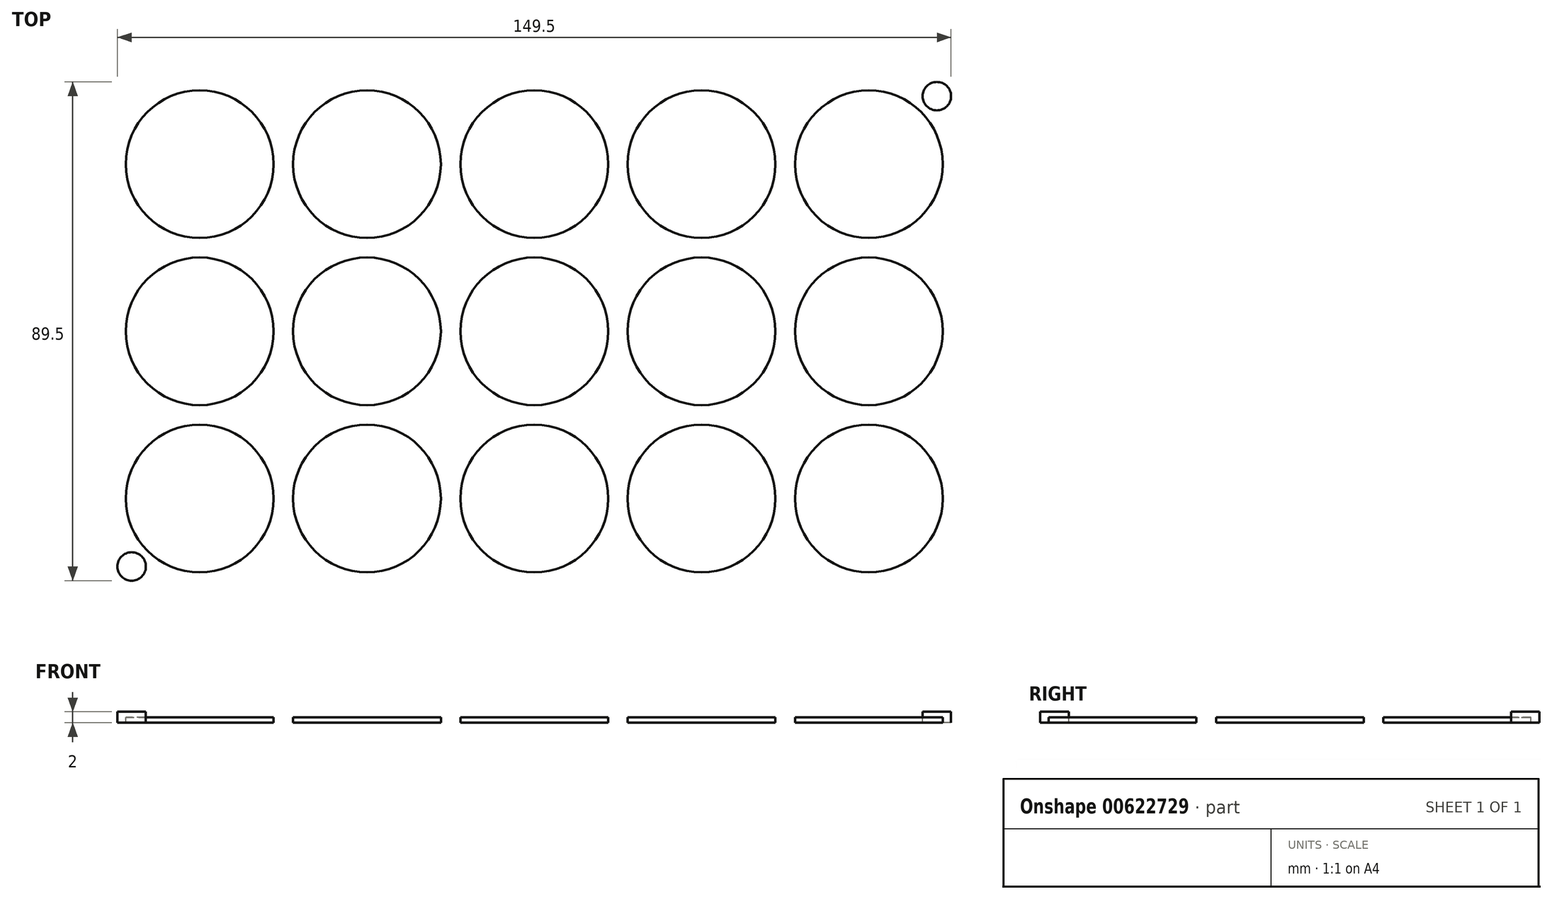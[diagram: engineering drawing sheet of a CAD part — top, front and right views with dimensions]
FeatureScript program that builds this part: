
annotation { "Feature Type Name" : "Feature", "Feature Type Description" : "" }
export const myFeature = defineFeature(function(context is Context, id is Id, definition is map)
    precondition{}
    {
        {
            var Q0;
            Q0=qCreatedBy(makeId("Top.planeOp"),FACE);
            var sketch = newSketch(context, id + "F0", { "sketchPlane" : qUnion([Q0])});
            skLineSegment(sketch, "E0.bottom", {"start": v(-76.25, 46.25) * mm, "end": v(76.25, 46.25) * mm});
            skLineSegment(sketch, "E0.top", {"start": v(-76.25, -46.25) * mm, "end": v(76.25, -46.25) * mm});
            skLineSegment(sketch, "E0.left", {"start": v(-76.25, 46.25) * mm, "end": v(-76.25, -46.25) * mm});
            skLineSegment(sketch, "E0.right", {"start": v(76.25, 46.25) * mm, "end": v(76.25, -46.25) * mm});
            skPoint(sketch, "E0.middle", {"position": v(0, 0) * mm});
            skCircle(sketch, "E1", {"center": v(-60, 30) * mm, "radius": 13.25 * mm});
            skCircle(sketch, "E2.0.1.0", {"center": v(-60, 0) * mm, "radius": 13.25 * mm});
            skCircle(sketch, "E2.0.2.0", {"center": v(-60, -30) * mm, "radius": 13.25 * mm});
            skCircle(sketch, "E2.1.0.0", {"center": v(-30, 30) * mm, "radius": 13.25 * mm});
            skCircle(sketch, "E2.1.1.0", {"center": v(-30, 0) * mm, "radius": 13.25 * mm});
            skCircle(sketch, "E2.1.2.0", {"center": v(-30, -30) * mm, "radius": 13.25 * mm});
            skCircle(sketch, "E2.2.0.0", {"center": v(0, 30) * mm, "radius": 13.25 * mm});
            skCircle(sketch, "E2.2.1.0", {"center": v(0, 0) * mm, "radius": 13.25 * mm});
            skCircle(sketch, "E2.2.2.0", {"center": v(0, -30) * mm, "radius": 13.25 * mm});
            skCircle(sketch, "E2.3.0.0", {"center": v(30, 30) * mm, "radius": 13.25 * mm});
            skCircle(sketch, "E2.3.1.0", {"center": v(30, 0) * mm, "radius": 13.25 * mm});
            skCircle(sketch, "E2.3.2.0", {"center": v(30, -30) * mm, "radius": 13.25 * mm});
            skCircle(sketch, "E2.4.0.0", {"center": v(60, 30) * mm, "radius": 13.25 * mm});
            skCircle(sketch, "E2.4.1.0", {"center": v(60, 0) * mm, "radius": 13.25 * mm});
            skCircle(sketch, "E2.4.2.0", {"center": v(60, -30) * mm, "radius": 13.25 * mm});
            skLineSegment(sketch, "E2.direction1", {"start": v(-60, 30) * mm, "end": v(-30, 30) * mm, "construction": true});
            skLineSegment(sketch, "E2.direction2", {"start": v(-60, 30) * mm, "end": v(-60, 0) * mm, "construction": true});
            skSolve(sketch);
        }
        {
            var Q0;
            Q0=makeQuery(id+"F0.imprint","IMPRINT",FACE,{"disambiguationData":[TD([[makeQuery(id+"F0.imprint","IMPRINT",EDGE,{"derivedFrom":sQuery(id+"F0.wireOp",EDGE,"E1")}),1.0]])]});
            var Q1;
            Q1=makeQuery(id+"F0.imprint","IMPRINT",FACE,{"disambiguationData":[TD([[makeQuery(id+"F0.imprint","IMPRINT",EDGE,{"derivedFrom":sQuery(id+"F0.wireOp",EDGE,"E2.1.0.0")}),1.0]])]});
            var Q2;
            Q2=makeQuery(id+"F0.imprint","IMPRINT",FACE,{"disambiguationData":[TD([[makeQuery(id+"F0.imprint","IMPRINT",EDGE,{"derivedFrom":sQuery(id+"F0.wireOp",EDGE,"E2.2.0.0")}),1.0]])]});
            var Q3;
            Q3=makeQuery(id+"F0.imprint","IMPRINT",FACE,{"disambiguationData":[TD([[makeQuery(id+"F0.imprint","IMPRINT",EDGE,{"derivedFrom":sQuery(id+"F0.wireOp",EDGE,"E2.3.0.0")}),1.0]])]});
            var Q4;
            Q4=makeQuery(id+"F0.imprint","IMPRINT",FACE,{"disambiguationData":[TD([[makeQuery(id+"F0.imprint","IMPRINT",EDGE,{"derivedFrom":sQuery(id+"F0.wireOp",EDGE,"E2.4.0.0")}),1.0]])]});
            var Q5;
            Q5=makeQuery(id+"F0.imprint","IMPRINT",FACE,{"disambiguationData":[TD([[makeQuery(id+"F0.imprint","IMPRINT",EDGE,{"derivedFrom":sQuery(id+"F0.wireOp",EDGE,"E2.4.1.0")}),1.0]])]});
            var Q6;
            Q6=makeQuery(id+"F0.imprint","IMPRINT",FACE,{"disambiguationData":[TD([[makeQuery(id+"F0.imprint","IMPRINT",EDGE,{"derivedFrom":sQuery(id+"F0.wireOp",EDGE,"E2.3.1.0")}),1.0]])]});
            var Q7;
            Q7=makeQuery(id+"F0.imprint","IMPRINT",FACE,{"disambiguationData":[TD([[makeQuery(id+"F0.imprint","IMPRINT",EDGE,{"derivedFrom":sQuery(id+"F0.wireOp",EDGE,"E0.bottom")}),-1.0]])]});
            var Q8;
            Q8=makeQuery(id+"F0.imprint","IMPRINT",FACE,{"disambiguationData":[TD([[makeQuery(id+"F0.imprint","IMPRINT",EDGE,{"derivedFrom":sQuery(id+"F0.wireOp",EDGE,"E2.1.1.0")}),1.0]])]});
            var Q9;
            Q9=makeQuery(id+"F0.imprint","IMPRINT",FACE,{"disambiguationData":[TD([[makeQuery(id+"F0.imprint","IMPRINT",EDGE,{"derivedFrom":sQuery(id+"F0.wireOp",EDGE,"E2.0.1.0")}),1.0]])]});
            var Q10;
            Q10=makeQuery(id+"F0.imprint","IMPRINT",FACE,{"disambiguationData":[TD([[makeQuery(id+"F0.imprint","IMPRINT",EDGE,{"derivedFrom":sQuery(id+"F0.wireOp",EDGE,"E2.2.1.0")}),1.0]])]});
            var Q11;
            Q11=makeQuery(id+"F0.imprint","IMPRINT",FACE,{"disambiguationData":[TD([[makeQuery(id+"F0.imprint","IMPRINT",EDGE,{"derivedFrom":sQuery(id+"F0.wireOp",EDGE,"E2.2.2.0")}),1.0]])]});
            var Q12;
            Q12=makeQuery(id+"F0.imprint","IMPRINT",FACE,{"disambiguationData":[TD([[makeQuery(id+"F0.imprint","IMPRINT",EDGE,{"derivedFrom":sQuery(id+"F0.wireOp",EDGE,"E2.1.2.0")}),1.0]])]});
            var Q13;
            Q13=makeQuery(id+"F0.imprint","IMPRINT",FACE,{"disambiguationData":[TD([[makeQuery(id+"F0.imprint","IMPRINT",EDGE,{"derivedFrom":sQuery(id+"F0.wireOp",EDGE,"E2.0.2.0")}),1.0]])]});
            var Q14;
            Q14=makeQuery(id+"F0.imprint","IMPRINT",FACE,{"disambiguationData":[TD([[makeQuery(id+"F0.imprint","IMPRINT",EDGE,{"derivedFrom":sQuery(id+"F0.wireOp",EDGE,"E2.3.2.0")}),1.0]])]});
            var Q15;
            Q15=makeQuery(id+"F0.imprint","IMPRINT",FACE,{"disambiguationData":[TD([[makeQuery(id+"F0.imprint","IMPRINT",EDGE,{"derivedFrom":sQuery(id+"F0.wireOp",EDGE,"E2.4.2.0")}),1.0]])]});
            var Q16;
            Q16=makeQuery(id+"F0.imprint","IMPRINT",FACE,{"disambiguationData":[TD([[makeQuery(id+"F0.imprint","IMPRINT",EDGE,{"derivedFrom":sQuery(id+"F0.wireOp",EDGE,"E2.3.3.0")}),1.0]])]});
            var Q17;
            Q17=makeQuery(id+"F0.imprint","IMPRINT",FACE,{"disambiguationData":[TD([[makeQuery(id+"F0.imprint","IMPRINT",EDGE,{"derivedFrom":sQuery(id+"F0.wireOp",EDGE,"E2.4.3.0")}),1.0]])]});
            var Q18;
            Q18=makeQuery(id+"F0.imprint","IMPRINT",FACE,{"disambiguationData":[TD([[makeQuery(id+"F0.imprint","IMPRINT",EDGE,{"derivedFrom":sQuery(id+"F0.wireOp",EDGE,"E2.4.4.0")}),1.0]])]});
            var Q19;
            Q19=makeQuery(id+"F0.imprint","IMPRINT",FACE,{"disambiguationData":[TD([[makeQuery(id+"F0.imprint","IMPRINT",EDGE,{"derivedFrom":sQuery(id+"F0.wireOp",EDGE,"E2.3.4.0")}),1.0]])]});
            var Q20;
            Q20=makeQuery(id+"F0.imprint","IMPRINT",FACE,{"disambiguationData":[TD([[makeQuery(id+"F0.imprint","IMPRINT",EDGE,{"derivedFrom":sQuery(id+"F0.wireOp",EDGE,"E2.2.4.0")}),1.0]])]});
            var Q21;
            Q21=makeQuery(id+"F0.imprint","IMPRINT",FACE,{"disambiguationData":[TD([[makeQuery(id+"F0.imprint","IMPRINT",EDGE,{"derivedFrom":sQuery(id+"F0.wireOp",EDGE,"E2.2.3.0")}),1.0]])]});
            var Q22;
            Q22=makeQuery(id+"F0.imprint","IMPRINT",FACE,{"disambiguationData":[TD([[makeQuery(id+"F0.imprint","IMPRINT",EDGE,{"derivedFrom":sQuery(id+"F0.wireOp",EDGE,"E2.1.4.0")}),1.0]])]});
            var Q23;
            Q23=makeQuery(id+"F0.imprint","IMPRINT",FACE,{"disambiguationData":[TD([[makeQuery(id+"F0.imprint","IMPRINT",EDGE,{"derivedFrom":sQuery(id+"F0.wireOp",EDGE,"E2.1.3.0")}),1.0]])]});
            var Q24;
            Q24=makeQuery(id+"F0.imprint","IMPRINT",FACE,{"disambiguationData":[TD([[makeQuery(id+"F0.imprint","IMPRINT",EDGE,{"derivedFrom":sQuery(id+"F0.wireOp",EDGE,"E2.0.3.0")}),1.0]])]});
            var Q25;
            Q25=makeQuery(id+"F0.imprint","IMPRINT",FACE,{"disambiguationData":[TD([[makeQuery(id+"F0.imprint","IMPRINT",EDGE,{"derivedFrom":sQuery(id+"F0.wireOp",EDGE,"E2.0.4.0")}),1.0]])]});
            extrude(context, id + "F1", {"entities" : qUnion([Q0, Q1, Q2, Q3, Q4, Q5, Q6, Q7, Q8, Q9, Q10, Q11, Q12, Q13, Q14, Q15, Q16, Q17, Q18, Q19, Q20, Q21, Q22, Q23, Q24, Q25]), "depth" : 1 * mm, "offsetDistance" : 25 * mm});
        }
        {
            var Q0;
            Q0=qSketchRegion(id+"F0",true);
            extrude(context, id + "F2", {"entities" : qUnion([Q0]), "operationType" : NewBodyOperationType.ADD, "depth" : 2 * mm, "offsetDistance" : 25 * mm});
        }
        {
            var Q0;
            Q0=makeQuery(id+"F2.opExtrude","CAP_FACE",FACE,{"disambiguationData":[OSD([sQuery(id+"F0.wireOp",EDGE,"E0.bottom"),sQuery(id+"F0.wireOp",EDGE,"E0.top"),sQuery(id+"F0.wireOp",EDGE,"E0.left"),sQuery(id+"F0.wireOp",EDGE,"E0.right"),sQuery(id+"F0.wireOp",EDGE,"E1"),sQuery(id+"F0.wireOp",EDGE,"E2.0.1.0"),sQuery(id+"F0.wireOp",EDGE,"E2.0.2.0"),sQuery(id+"F0.wireOp",EDGE,"E2.0.3.0"),sQuery(id+"F0.wireOp",EDGE,"E2.0.4.0"),sQuery(id+"F0.wireOp",EDGE,"E2.1.0.0"),sQuery(id+"F0.wireOp",EDGE,"E2.1.1.0"),sQuery(id+"F0.wireOp",EDGE,"E2.1.2.0"),sQuery(id+"F0.wireOp",EDGE,"E2.1.3.0"),sQuery(id+"F0.wireOp",EDGE,"E2.1.4.0"),sQuery(id+"F0.wireOp",EDGE,"E2.2.0.0"),sQuery(id+"F0.wireOp",EDGE,"E2.2.1.0"),sQuery(id+"F0.wireOp",EDGE,"E2.2.2.0"),sQuery(id+"F0.wireOp",EDGE,"E2.2.3.0"),sQuery(id+"F0.wireOp",EDGE,"E2.2.4.0"),sQuery(id+"F0.wireOp",EDGE,"E2.3.0.0"),sQuery(id+"F0.wireOp",EDGE,"E2.3.1.0"),sQuery(id+"F0.wireOp",EDGE,"E2.3.2.0"),sQuery(id+"F0.wireOp",EDGE,"E2.3.3.0"),sQuery(id+"F0.wireOp",EDGE,"E2.3.4.0"),sQuery(id+"F0.wireOp",EDGE,"E2.4.0.0"),sQuery(id+"F0.wireOp",EDGE,"E2.4.1.0"),sQuery(id+"F0.wireOp",EDGE,"E2.4.2.0"),sQuery(id+"F0.wireOp",EDGE,"E2.4.3.0"),sQuery(id+"F0.wireOp",EDGE,"E2.4.4.0")])],"isStart":false});
            var sketch = newSketch(context, id + "F3", { "sketchPlane" : qUnion([Q0])});
            skLineSegment(sketch, "E3", {"start": v(0, 74.2) * mm, "end": v(0, -73.43) * mm, "construction": true});
            skLineSegment(sketch, "E4", {"start": v(-81.9, 0) * mm, "end": v(78.5, 0) * mm, "construction": true});
            skCircle(sketch, "E5", {"center": v(-72.2, 42.2) * mm, "radius": 2.55 * mm});
            skCircle(sketch, "E6.MirrorC", {"center": v(72.2, 42.2) * mm, "radius": 2.55 * mm});
            skCircle(sketch, "E7.MirrorC", {"center": v(72.2, -42.2) * mm, "radius": 2.55 * mm});
            skCircle(sketch, "E8.MirrorC", {"center": v(-72.2, -42.2) * mm, "radius": 2.55 * mm});
            skCircle(sketch, "E9", {"center": v(-15, 15) * mm, "radius": 2.55 * mm});
            skCircle(sketch, "E10", {"center": v(15, -15) * mm, "radius": 2.55 * mm});
            skSolve(sketch);
        }
        {
            var Q0;
            Q0=makeQuery(id+"F3.imprint","IMPRINT",FACE,{"disambiguationData":[TD([[makeQuery(id+"F3.imprint","IMPRINT",EDGE,{"derivedFrom":sQuery(id+"F3.wireOp",EDGE,"E5")}),1.0]])]});
            var Q1;
            Q1=makeQuery(id+"F3.imprint","IMPRINT",FACE,{"disambiguationData":[TD([[makeQuery(id+"F3.imprint","IMPRINT",EDGE,{"derivedFrom":sQuery(id+"F3.wireOp",EDGE,"E6.MirrorC")}),-1.0]])]});
            var Q2;
            Q2=makeQuery(id+"F3.imprint","IMPRINT",FACE,{"disambiguationData":[TD([[makeQuery(id+"F3.imprint","IMPRINT",EDGE,{"derivedFrom":sQuery(id+"F3.wireOp",EDGE,"2e68c3d5-25cd-40bd-9945-6fc11be80f0a0.MirrorC")}),-1.0]])]});
            var Q3;
            Q3=makeQuery(id+"F3.imprint","IMPRINT",FACE,{"disambiguationData":[TD([[makeQuery(id+"F3.imprint","IMPRINT",EDGE,{"derivedFrom":sQuery(id+"F3.wireOp",EDGE,"QxaMrl3A-AtRa-trL4-GzdF-NhNgddZBNQFQ")}),1.0]])]});
            var Q4;
            Q4=makeQuery(id+"F3.imprint","IMPRINT",FACE,{"disambiguationData":[TD([[makeQuery(id+"F3.imprint","IMPRINT",EDGE,{"derivedFrom":sQuery(id+"F3.wireOp",EDGE,"839e4620-8980-43f4-94e8-6378de930a700.MirrorC")}),1.0]])]});
            var Q5;
            Q5=makeQuery(id+"F3.imprint","IMPRINT",FACE,{"disambiguationData":[TD([[makeQuery(id+"F3.imprint","IMPRINT",EDGE,{"derivedFrom":sQuery(id+"F3.wireOp",EDGE,"e168a04d-0960-4fc3-8a07-1196803d19df0.MirrorC")}),-1.0]])]});
            var Q6;
            Q6=makeQuery(id+"F3.imprint","IMPRINT",FACE,{"disambiguationData":[TD([[makeQuery(id+"F3.imprint","IMPRINT",EDGE,{"derivedFrom":sQuery(id+"F3.wireOp",EDGE,"E8.MirrorC")}),-1.0]])]});
            var Q7;
            Q7=makeQuery(id+"F3.imprint","IMPRINT",FACE,{"disambiguationData":[TD([[makeQuery(id+"F3.imprint","IMPRINT",EDGE,{"derivedFrom":sQuery(id+"F3.wireOp",EDGE,"E7.MirrorC")}),1.0]])]});
            var Q8;
            Q8=makeQuery(id+"F3.imprint","IMPRINT",FACE,{"disambiguationData":[TD([[makeQuery(id+"F3.imprint","IMPRINT",EDGE,{"derivedFrom":sQuery(id+"F3.wireOp",EDGE,"E10")}),1.0]])]});
            var Q9;
            Q9=makeQuery(id+"F3.imprint","IMPRINT",FACE,{"disambiguationData":[TD([[makeQuery(id+"F3.imprint","IMPRINT",EDGE,{"derivedFrom":sQuery(id+"F3.wireOp",EDGE,"E9")}),1.0]])]});
            extrude(context, id + "F4", {"entities" : qUnion([Q0, Q1, Q2, Q3, Q4, Q5, Q6, Q7, Q8, Q9]), "operationType" : NewBodyOperationType.REMOVE, "endBound" : BoundingType.THROUGH_ALL, "oppositeDirection" : true, "depth" : 25 * mm, "offsetDistance" : 25 * mm});
        }
    });
